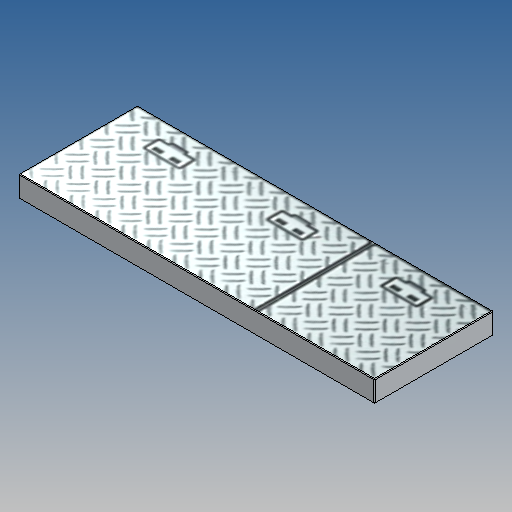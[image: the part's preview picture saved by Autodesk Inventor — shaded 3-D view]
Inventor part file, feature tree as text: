
AUTODESK INVENTOR PART (.ipt)
format: ipt  version: 2025 (Build 290162010, 162A)  size: 367,104 bytes
history: native  units: in
note: dims shown in document units (in); Inventor stores cm internally (conversion verified against a paired STEP export)
features: other x6, extrude x3, sketch x2, fillet x1, projected_geometry x1
ambient origin geometry x8: Origin, YZ Plane, XZ Plane, XY Plane, X Axis, Y Axis, Z Axis, Center Point
bodies: Solid1 (feature_tree)
feature tree (13):
  sketch  "Sketch2"  dims[d0=0.6299in d1=1.8898in]
  extrude  "Extrusion1"  Depth=1.8898in
  extrude  "Extrusion2"  Depth=0.0157in
  extrude  "Extrusion3"  Depth=0.0039in
  fillet  "Fillet1"  Radius=0.252in
  other  "Work Axis1"
  other  "Work Axis2"
  other  "Work Axis3"
  other  "Work Axis4"
  other  "Aufkleber1"
  sketch  "Skizze3"  dims[d2=0.0157in d3=0.0157in d4=0.189in d5=0.252in d6=0.315in d7=0.063in d8=0.063in d9=0.126in d10=0.0in d11=0.0157in d12=0.0in d13=0.063in d14=0.0in d15=0.189in d16=0.0039in d17=0.0in d18=0.0in d19=0.0in d20=0.0in d21=0.0in d22=0.0in d23=0.0in d49=0.0354in d50=0.0276in]
  projected_geometry  "Projizierte Kontur1"
  other  "Bild3"
